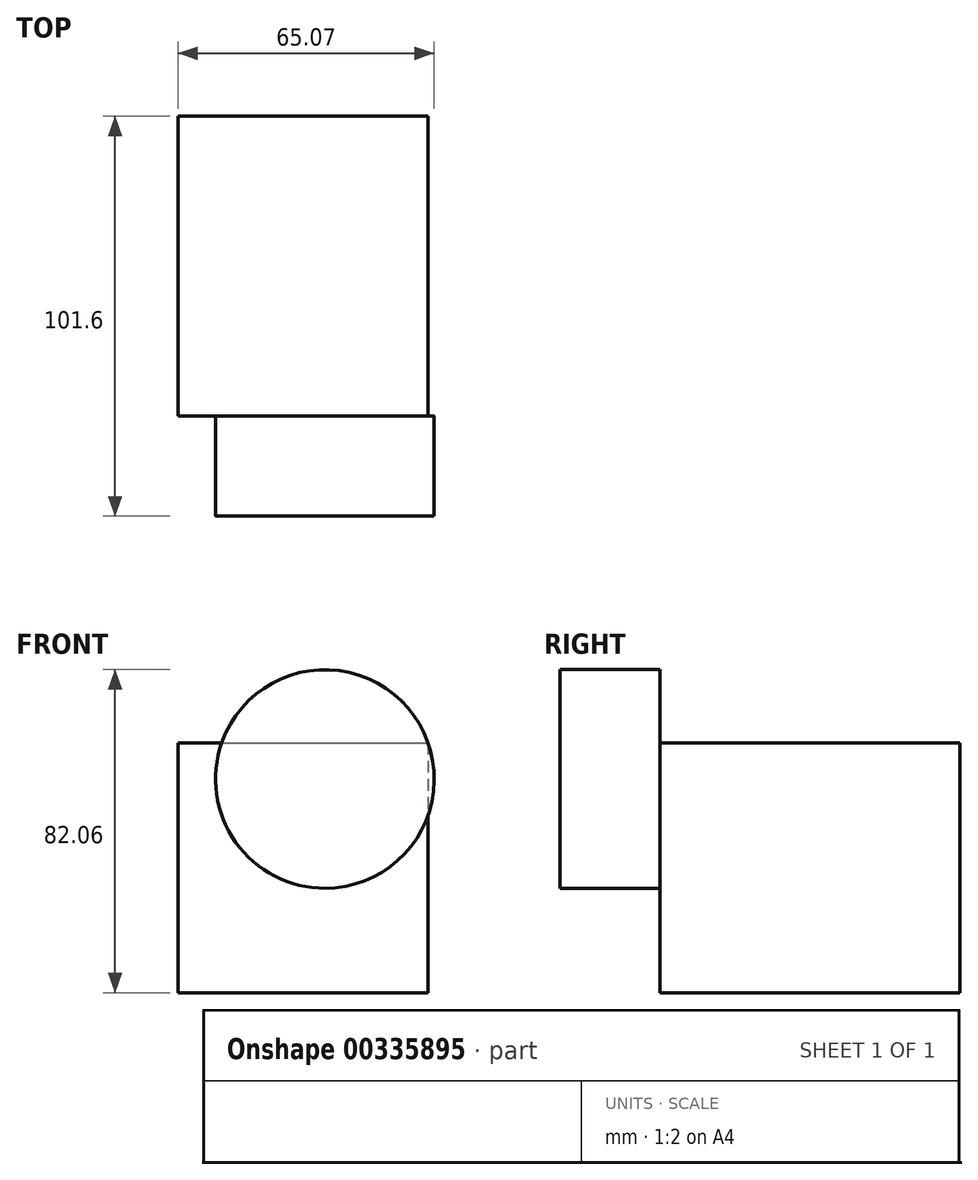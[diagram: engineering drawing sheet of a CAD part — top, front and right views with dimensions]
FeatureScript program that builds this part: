
annotation { "Feature Type Name" : "Feature", "Feature Type Description" : "" }
export const myFeature = defineFeature(function(context is Context, id is Id, definition is map)
    precondition{}
    {
        {
            var Q0;
            Q0=qCreatedBy(makeId("Front.planeOp"),FACE);
            var sketch = newSketch(context, id + "F0", { "sketchPlane" : qUnion([Q0])});
            skLineSegment(sketch, "E0", {"start": v(0, 0) * mm, "end": v(0, 63.5) * mm});
            skLineSegment(sketch, "E1", {"start": v(0, 63.5) * mm, "end": v(63.5, 63.5) * mm});
            skLineSegment(sketch, "E2", {"start": v(63.5, 63.5) * mm, "end": v(63.5, 0) * mm});
            skLineSegment(sketch, "E3", {"start": v(63.5, 0) * mm, "end": v(0, 0) * mm});
            skSolve(sketch);
        }
        {
            var Q0;
            Q0=makeQuery(id+"F0.imprint","IMPRINT",FACE,{"disambiguationData":[TD([[makeQuery(id+"F0.imprint","IMPRINT",EDGE,{"derivedFrom":sQuery(id+"F0.wireOp",EDGE,"E0")}),-1.0]])]});
            extrude(context, id + "F1", {"entities" : qUnion([Q0]), "depth" : 76.2 * mm});
        }
        {
            var Q0;
            Q0=makeQuery(id+"F1.opExtrude","CAP_FACE",FACE,{"disambiguationData":[OSD([sQuery(id+"F0.wireOp",EDGE,"E0"),sQuery(id+"F0.wireOp",EDGE,"E1"),sQuery(id+"F0.wireOp",EDGE,"E2"),sQuery(id+"F0.wireOp",EDGE,"E3")])],"isStart":false});
            var sketch = newSketch(context, id + "F2", { "sketchPlane" : qUnion([Q0])});
            skCircle(sketch, "E4", {"center": v(37.3, 54.28) * mm, "radius": 27.78 * mm});
            skPoint(sketch, "E4.first.point", {"position": v(12.22, 42.35) * mm});
            skPoint(sketch, "E4.second.point", {"position": v(47.96, 28.63) * mm});
            skPoint(sketch, "E4.third.point", {"position": v(63.5, 63.5) * mm});
            skSolve(sketch);
        }
        {
            var Q0;
            Q0 = qSketchRegion(id + "F2", true);
            extrude(context, id + "F3", {"entities" : qUnion([Q0]), "operationType" : NewBodyOperationType.ADD, "depth" : 25.4 * mm});
        }
    });
